# Revit family: NaughtOne_SymbolThreeSeatWork
name_source: partatom
category: Furniture
units: mm (PartAtom-declared; Revit-internal decimal feet)

## family parameters
Always vertical = Yes
Cut with Voids When Loaded = No
Enable Cutting in Views = No
OmniClass Number = 23.40.20.00
OmniClass Title = General Furniture and Specialties
Render Appearance Source = Family Geometry
Room Calculation Point = No
Shared = Yes
Work Plane-Based = No

## types (9) — shared parameters
Assembly Code = E2020200
Manufacturer = Herman Miller, Inc.
Package Qty = 1
URL = http://www.hermanmiller.com
zero-valued in all types: Default Elevation

## per-type parameters (varying)
| type | Description | Foot aux 1 | Foot aux 2 | Foot aux 3 | Foot aux 4 | Model | Seat Aux | Seat Bench Single Fabric | Seat Left Arm Single and Multiple Fabric | Seat No Arms Single and Multiple Fabric | Seat Right Arm Single and Multiple Fabric | Seat Two Arms Single and Multiple Fabric | Type |
| Seat Bench Single Fabric Work Ht | Symbol Three Seat Bench Work height 18 inch seat height Single Fabric | 9.634 " | 37.4 " | 38.5 " | 9.634 " | NOSYN310W1 | 30.2 " | Yes | No | No | No | No | 1 |
| Seat No Arms Single Fabric Work Ht | Symbol Three Seat Bench Work height 18 inch seat height Single Fabric | 9.68 " | 7.1 " | 68.63 " | 16.65 " | NOSYN320W1 | 60.3 " | No | No | Yes | No | No | 2 |
| Seat No Arms Multiple Fabric Work Ht | Symbol Three Seat No Arms Work height 18 inch seat height Multiple Fabric | 9.68 " | 7.1 " | 68.63 " | 16.65 " | NOSYN320W2 | 60.3 " | No | No | Yes | No | No | 3 |
| Seat Right Arm Single Fabric Work Ht | Symbol Three Seat Right Arm Work height 18 inch seat height Single Fabric | 9.7 " | 67.55 " | 1.114 " | 16.7 " | NOSYN330W1 | 0 " | No | Yes | No | No | No | 4 |
| Seat Right Arm Multiple Fabric Work Ht | Symbol Three Seat Right Arm Work height 18 inch seat height Multiple Fabric | 9.7 " | 67.55 " | 1.114 " | 16.7 " | NOSYN330W2 | 0 " | No | Yes | No | No | No | 5 |
| Seat Left Arm Single Fabric Work Ht | Symbol Three Seat Left Arm Work height 18 inch seat height Single Fabric | 9.7 " | 0.2 " | 68.54 " | 16.65 " | NOSYN340W1 | 60.3 " | No | No | No | Yes | No | 6 |
| Seat Left Arm Multiple Fabric Work Ht | Symbol Three Seat Left Arm Work height 18 inch seat height Multiple Fabric | 9.7 " | 0.2 " | 68.54 " | 16.65 " | NOSYN340W2 | 60.3 " | No | No | No | Yes | No | 7 |
| Seat Two Arms Single Fabric Work Ht | Symbol Three Seat Two Arms Work height 18 inch seat height Single Fabric | 9.7 " | 30.3 " | 31.3 " | 16.65 " | NOSYN350W1 | 30.2 " | No | No | No | No | Yes | 8 |
| Seat Two Arms Multiple Fabric Work Ht | Symbol Three Seat Two Arms Work height 18 inch seat height Multiple Fabric | 9.7 " | 30.3 " | 31.3 " | 16.65 " | NOSYN350W2 | 30.2 " | No | No | No | No | Yes | 9 |

## geometry (parser evidence)
native form markers: Sweep x10
no freeform markers — native parametric forms only
